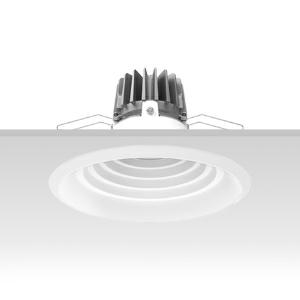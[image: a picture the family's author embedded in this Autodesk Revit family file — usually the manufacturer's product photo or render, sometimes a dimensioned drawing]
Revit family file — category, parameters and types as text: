
# Revit family: 3f_filippi_-_3f_reno_bianco_ugr_3f_filippi_-_30753_-_3f_reno_200_wh_2000-840_dali_ugr
name_source: partatom
category: Lighting Fixtures
units: mm (PartAtom-declared; Revit-internal decimal feet)

## family parameters
Cut with Voids When Loaded = No
Host = Face
Light Source = No
Part Type = Normal
Room Calculation Point = No
Round Connector Dimension = Use Diameter
Shared = No

## types (1)
- 3F Filippi - 3F Reno Bianco UGR (1 x LED, 2458 lm, 20 W, 4000 K)
    Apparent Load = 20 VA
    Approval mark = CE
    CIE Flux Codes = 90 100 100 100 100
    Color Rendering = 80
    Color Temperature = 4000 K
    Control Gear = Electronic transformer
    Default Elevation = 1800 mm
    Description = ILLUMINOTECHNICAL
Luminous efficiency 100% (DLOR 100%, ULOR 0%).
Initial luminous flux of the luminaire 2458 lm.
Direct symmetric UGR distribution.
Installation Interdistance Transv.D = 0.99 x hu - Long.D = 1.01 x hu.
Average luminance <500 cd/m² for radial angles >65°.
Tabular UGR (CIE 117 - 4H-8H; S=0.25H; 70/50/20): RUG 17.4 - 17.3.
Beam angle: 64° - 65°.
Luminous efficacy 123 lm/W.
Lifetime (L90/B10): 30000 h. (tq+25°C)
Lifetime (L85/B10): 50000 h. (tq+25°C)
Lifetime (L70/B10): 80000 h. (tq+25°C)
Sudden decreased luminous flux after 50000 hours: 0% (C0).
Photobiological safety in compliance with IEC/TR 62778: RG0 risk exempt, (IEC 62471).
In compliance with IEC/EN 62722-2-1 - IEC/EN 62717 standards.

SOURCE
Compact LED module 2000/840.
Energy efficiency class (UE 2019/2020 - UE 2019/2015): D.
CIE 13.3 Colour rendering index: CRI >80 (R9 <50%).
IES TM-30 Fidelity Index: Rf = 84 Rg = 95.
CCT nominal colour temperature 4000 K.
Colour initial tolerance (MacAdam): SDCM 3.
Zhaga Book 3 compliant.

MECHANICAL
Passive heat dissipator in die-casting aluminium, oversized, for optimum thermal management of the LED module.
Parabolic element with graduated/concentric rings in white polycarbonate.
Internal specular metallic louvre to optimise control of the luminous flux in polycarbonate.
Transparent external lens with glossy and satin differentiated surfaces, with a cooling and anti-insect system in methacrylate (PMMA).
Fastening spring clips in stainless steel.
Dimensions: diameter 216 mm, height 142 mm. Weight 0.85 kg.
IP44 protection degree for exposed part, IP20 for recessed part.
Mechanical strength to impacts IK04 (0.5 joule).
Glow-wire test resistance 650°C.

ELECTRICAL
Wiring on a separate unit.
Halogen Free DALI-2 DATI (Parts 251, 252, 253), PUSH-DIM, electronic wiring 230V-50/60Hz, power factor 0.90 at full load, THD <25%, constant output current, SELV, class II, 1 driver, 1 DALI addresse.
Power of the luminaire 20 W.
ENEC - CE.
SAFE FLICKER: PstLM=<1 and SVM=<0.4 (IEC TR 61547-1 and IEC TR 63158), to ensure a more comfortable and safe light.
Luminaire compliant with EN 60598-2-22 for power supply from a centralised emergency system CPSS (Central Power Supply System), not incorporated in the luminaire - high risk areas excluded. The default power and flux are 100% in AC and 100% in DC.
Ambient temperature from 0°C to +25°C.
Temperature class T6 max 85°C.
Relative humidity UR: <85%.

INSTALLATION
Pull-up recessed fitting.
False ceiling carving: 200 mm.
All accessories dedicated to this product are available on the Catalog and on our website www.3F-Filippi.com.

APPLICATIONS
In environments with VDTs, managerial offices and staterooms, public offices and schools.
In false ceilings with narrow voids.

LIGHT MANAGEMENT
Recommended minimum setting: 10%.
The luminaire, equipped with (DALI-2 DATI) driver, can be controlled manually with 3F Easy Dim technology or automatically/manually with wired or wireless DALI/D2D control systems.
The D2D driver guarantees interoperability with other devices with the same certification by making the following information available:
Device Data (Part 251), Energy Report (Part 252), Diagnosis & Maintenance (Part 253).
In electrical systems without a regulation system (manual or automatic) and DALI bus, a suitable jumper must be made on the DA-DA terminals of the appliance.

WARNING
Luminaire designed for disposal/recycling at end-of-life.
Replaceable (LED only) light source by a professional. Replaceable control gear by a professional.
    Height = 0 mm  [stored 0 ft]
    Lamp = 1 x LED
    Lamp Light Flux = 2458 lm
    Lamp Power = 20 W
    Lamp count = 1
    Length = 216 mm
    Lifetime = 50000 h
    Luminous efficacy = 123 lm/W
    Manufacturer = 3F Filippi
    ModVariant = No
    Model = 3F Filippi - 30753 - 3F Reno 200 WH 2000-840 DALI UGR
    Mounting Place = Ceiling
    Mounting Type = Recessed
    Number of Poles = 1
    OnlyDefault = Yes
    Power Factor = 1
    Product Name = 3F Filippi - 3F Reno Bianco UGR
    Product group = recessed luminaire
    ProductGroupID = 4
    Protection Class = Protection class II
    Protection Degree = IP 20
    RLX_Detail_Level = 1
    RLX_Emergency_Light_Flux = 0 lm
    RLX_Emergency_Type = 0
    RLX_Emergency_Type_DB = No
    RlxData = <blob elided: 90757 chars, md5=7c1e3b30>
    Socket = socket
    Standby Power = 0 W
    System Light Flux = 2458 lm
    System Power = 20 W
    Type Comments = Product without accessories
    Type Image = 3ffilippi_3f_reno_200_wh_2000.jpg
    URL = http://relux.com
    VarID = ---
    Voltage = 0 V
    Weight = 0.00 kg
    Width = 0 mm  [stored 0 ft]

note: [stored X ft] marks values corroborated as IEEE doubles in the binary element streams (Revit-internal decimal feet)

## geometry (parser evidence)
native form markers: Blend x4, Sweep x10
no freeform markers — native parametric forms only
